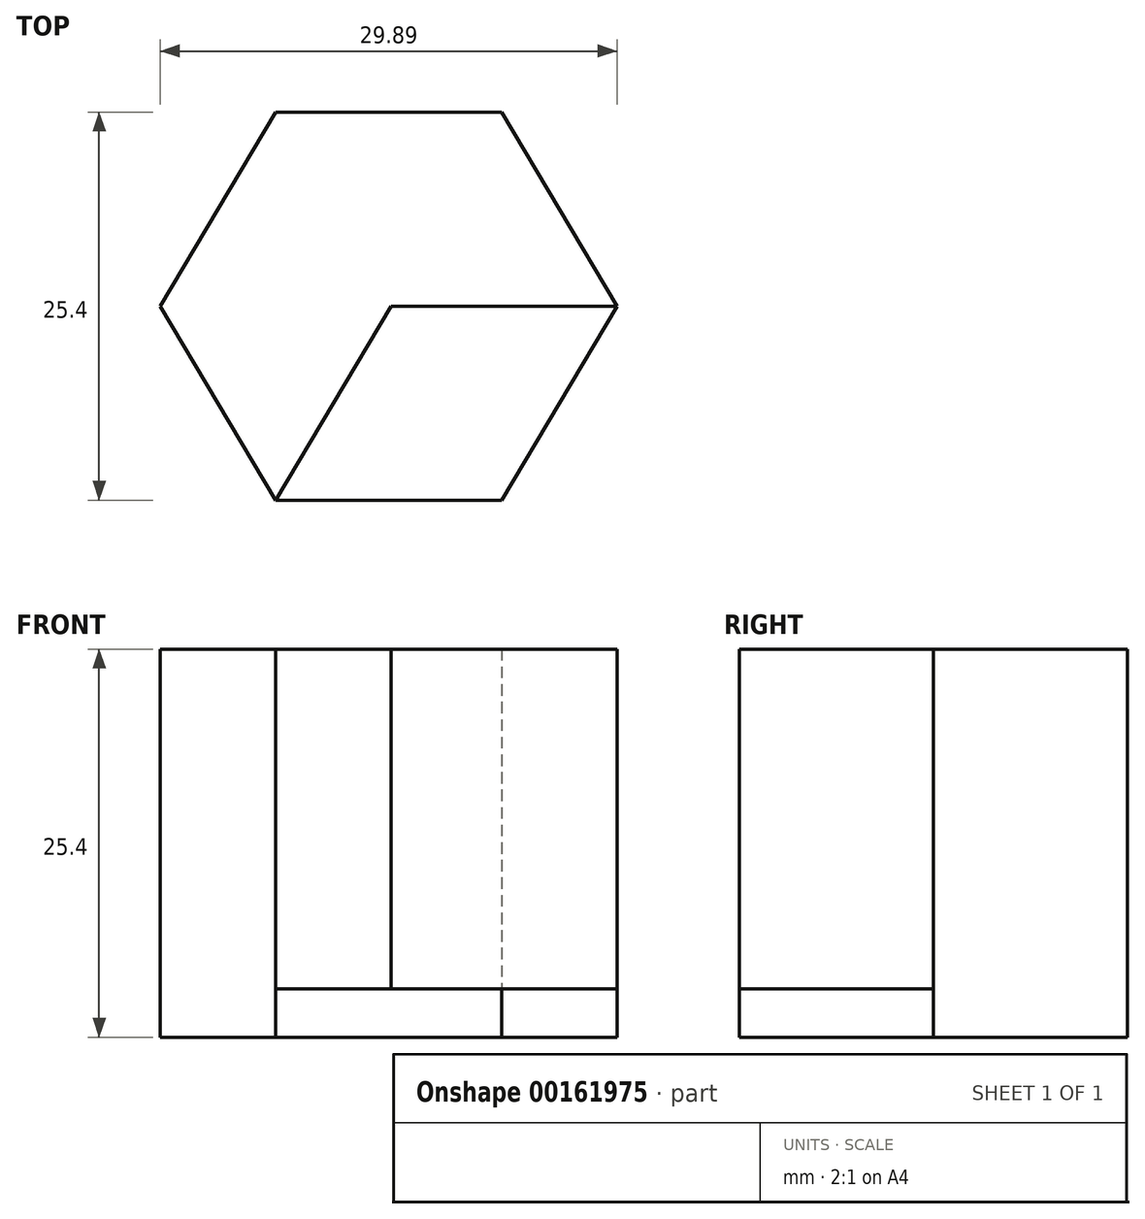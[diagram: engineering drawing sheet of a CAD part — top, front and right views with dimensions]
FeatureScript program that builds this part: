
annotation { "Feature Type Name" : "Feature", "Feature Type Description" : "" }
export const myFeature = defineFeature(function(context is Context, id is Id, definition is map)
    precondition{}
    {
        {
            var Q0;
            Q0=qCreatedBy(makeId("Top.planeOp"),FACE);
            var sketch = newSketch(context, id + "F0", { "sketchPlane" : qUnion([Q0])});
            skLineSegment(sketch, "E0", {"start": v(0, 0) * mm, "end": v(7.56, 12.7) * mm});
            skLineSegment(sketch, "E1", {"start": v(7.56, 12.7) * mm, "end": v(22.34, 12.7) * mm});
            skLineSegment(sketch, "E2", {"start": v(22.34, 12.7) * mm, "end": v(29.9, 0) * mm});
            skLineSegment(sketch, "E3", {"start": v(29.9, 0) * mm, "end": v(22.34, -12.7) * mm});
            skLineSegment(sketch, "E4", {"start": v(22.34, -12.7) * mm, "end": v(7.56, -12.7) * mm});
            skLineSegment(sketch, "E5", {"start": v(7.56, -12.7) * mm, "end": v(0, 0) * mm});
            skSolve(sketch);
        }
        {
            var Q0;
            Q0=makeQuery(id+"F0.imprint","IMPRINT",FACE,{"disambiguationData":[TD([[makeQuery(id+"F0.imprint","IMPRINT",EDGE,{"derivedFrom":sQuery(id+"F0.wireOp",EDGE,"E0")}),-1.0]])]});
            extrude(context, id + "F1", {"entities" : qUnion([Q0]), "depth" : 3.17 * mm});
        }
        {
            var Q0;
            Q0=makeQuery(id+"F1.opExtrude","CAP_FACE",FACE,{"disambiguationData":[OSD([sQuery(id+"F0.wireOp",EDGE,"E0"),sQuery(id+"F0.wireOp",EDGE,"E1"),sQuery(id+"F0.wireOp",EDGE,"E2"),sQuery(id+"F0.wireOp",EDGE,"E3"),sQuery(id+"F0.wireOp",EDGE,"E4"),sQuery(id+"F0.wireOp",EDGE,"E5")])],"isStart":false});
            var sketch = newSketch(context, id + "F2", { "sketchPlane" : qUnion([Q0])});
            skLineSegment(sketch, "E6", {"start": v(7.56, -12.7) * mm, "end": v(15.11, 0) * mm});
            skLineSegment(sketch, "E7", {"start": v(15.11, 0) * mm, "end": v(29.9, 0) * mm});
            skLineSegment(sketch, "E8", {"start": v(7.56, -12.7) * mm, "end": v(7.56, 0) * mm, "construction": true});
            skLineSegment(sketch, "E9", {"start": v(18.47, 6.2) * mm, "end": v(29.9, 0) * mm, "construction": true});
            skLineSegment(sketch, "E10", {"start": v(0, 0) * mm, "end": v(7.56, 0) * mm, "construction": true});
            skLineSegment(sketch, "E11", {"start": v(18.47, 6.2) * mm, "end": v(22.34, 12.7) * mm, "construction": true});
            skLineSegment(sketch, "E12", {"start": v(7.56, 0) * mm, "end": v(11.25, 6.2) * mm, "construction": true});
            skLineSegment(sketch, "E13", {"start": v(11.25, 6.2) * mm, "end": v(18.47, 6.2) * mm, "construction": true});
            skSolve(sketch);
        }
        {
            var Q0;
            Q0=makeQuery(id+"F2.imprint","IMPRINT",FACE,{"disambiguationData":[TD([[makeQuery(id+"F2.imprint","IMPRINT",EDGE,{"derivedFrom":sQuery(id+"F2.wireOp",EDGE,"E6")}),1.0]])]});
            extrude(context, id + "F3", {"entities" : qUnion([Q0]), "operationType" : NewBodyOperationType.ADD, "depth" : 22.22 * mm});
        }
    });
